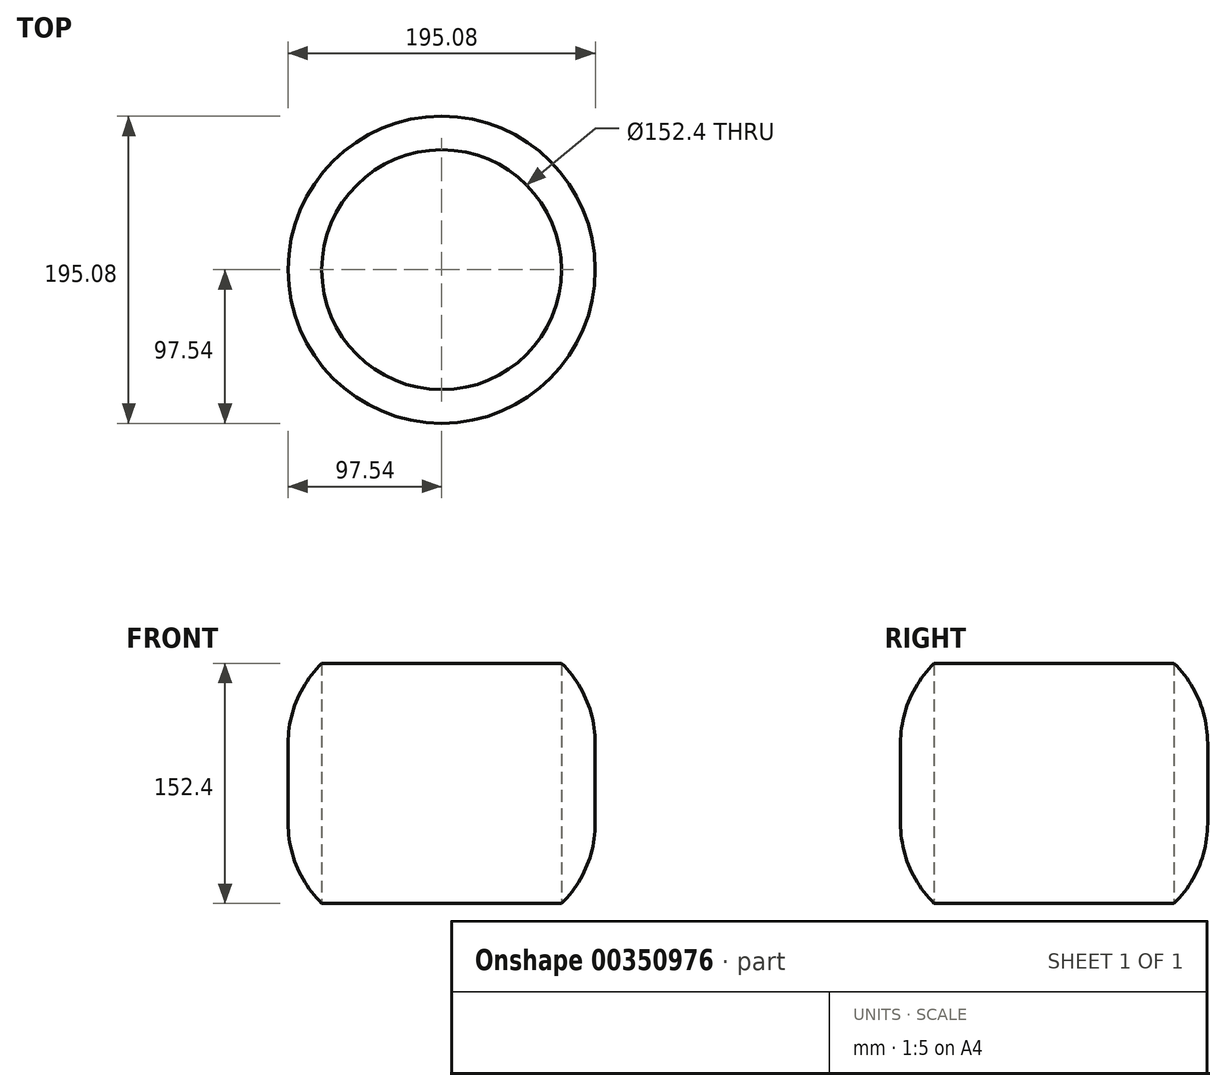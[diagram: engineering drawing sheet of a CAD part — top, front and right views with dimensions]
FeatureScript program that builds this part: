
annotation { "Feature Type Name" : "Feature", "Feature Type Description" : "" }
export const myFeature = defineFeature(function(context is Context, id is Id, definition is map)
    precondition{}
    {
        {
            var Q0;
            Q0=qCreatedBy(makeId("Top.planeOp"),FACE);
            var sketch = newSketch(context, id + "F0", { "sketchPlane" : qUnion([Q0])});
            skCircle(sketch, "E0", {"center": v(0, 0) * mm, "radius": 97.54 * mm});
            skCircle(sketch, "E1", {"center": v(0, 0) * mm, "radius": 76.2 * mm});
            skSolve(sketch);
        }
        {
            var Q0;
            Q0 = qSketchRegion(id + "F0", true);
            extrude(context, id + "F1", {"entities" : qUnion([Q0]), "depth" : 152.4 * mm});
        }
        {
            var Q0;
            Q0=makeQuery(id+"F1.opExtrude","CAP_EDGE",EDGE,{"disambiguationData":[OSD([sQuery(id+"F0.wireOp",EDGE,"E0")])],"isStart":false});
            fillet(context, id + "F2", {"entities" : qUnion([Q0]), "radius" : 71.12 * mm, "tangentPropagation" : true, "allowEdgeOverflow" : false});
        }
        {
            var Q0;
            Q0=makeQuery(id+"F1.opExtrude","SWEPT_FACE",FACE,{"disambiguationData":[OSD([sQuery(id+"F0.wireOp",EDGE,"E0")])]});
            fillet(context, id + "F3", {"entities" : qUnion([Q0]), "radius" : 71.12 * mm, "tangentPropagation" : true, "allowEdgeOverflow" : false});
        }
    });
